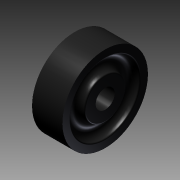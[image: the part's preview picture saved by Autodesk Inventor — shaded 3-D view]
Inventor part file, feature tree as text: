
AUTODESK INVENTOR PART (.ipt)
format: ipt  version: 2012 (Build 160160000, 160)  size: 175,104 bytes
history: native  units: in
note: dims shown in document units (in); Inventor stores cm internally (conversion verified against a paired STEP export)
features: revolve x1, fillet x1, sketch x1
ambient origin geometry x8: Origin, YZ Plane, XZ Plane, XY Plane, X Axis, Y Axis, Z Axis, Center Point
bodies: Solid1 (feature_tree)
feature tree (3):
  revolve  "Revolution1"  [1 undecoded]
  fillet  "Fillet1"  Radius=0.25in
  sketch  "Sketch1"  dims[d0=0.8in d1=0.875in d3=0.25in d4=0.4in d5=0.1875in d6=0.1875in d7=0.4in d8=90.0deg d9=0.0312in]
note: 1 required parameter value undecoded (feature->parameter linkage not recoverable at this tier; creation-order binding heuristic only, values carry confidence <= 0.55)
